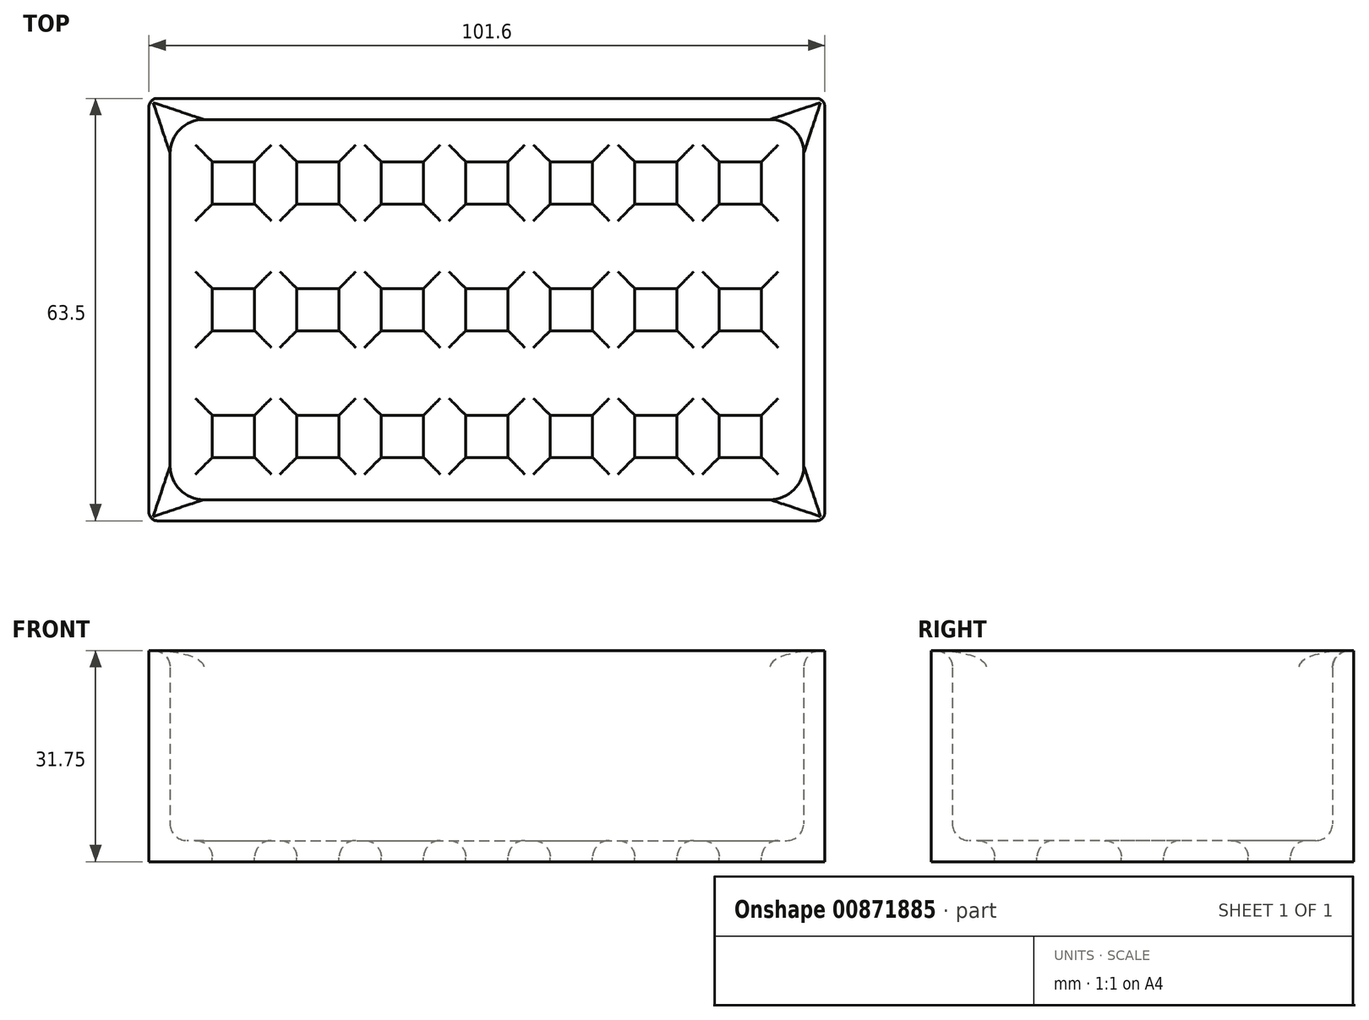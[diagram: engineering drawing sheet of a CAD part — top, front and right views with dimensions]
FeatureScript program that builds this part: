
annotation { "Feature Type Name" : "Feature", "Feature Type Description" : "" }
export const myFeature = defineFeature(function(context is Context, id is Id, definition is map)
    precondition{}
    {
        {
            var Q0;
            Q0=qCreatedBy(makeId("Top.planeOp"),FACE);
            var sketch = newSketch(context, id + "F0", { "sketchPlane" : qUnion([Q0])});
            skLineSegment(sketch, "E0.bottom", {"start": v(0, 0) * mm, "end": v(101.6, 0) * mm});
            skLineSegment(sketch, "E0.top", {"start": v(0, 63.5) * mm, "end": v(101.6, 63.5) * mm});
            skLineSegment(sketch, "E0.left", {"start": v(0, 0) * mm, "end": v(0, 63.5) * mm});
            skLineSegment(sketch, "E0.right", {"start": v(101.6, 0) * mm, "end": v(101.6, 63.5) * mm});
            skSolve(sketch);
        }
        {
            var Q0;
            Q0 = qSketchRegion(id + "F0", true);
            extrude(context, id + "F1", {"entities" : qUnion([Q0]), "depth" : 3.17 * mm, "offsetDistance" : 25.4 * mm});
        }
        {
            var Q0;
            Q0=makeQuery(id+"F1.opExtrude","CAP_FACE",FACE,{"disambiguationData":[OSD([sQuery(id+"F0.wireOp",EDGE,"E0.bottom"),sQuery(id+"F0.wireOp",EDGE,"E0.top"),sQuery(id+"F0.wireOp",EDGE,"E0.left"),sQuery(id+"F0.wireOp",EDGE,"E0.right")])],"isStart":false});
            var sketch = newSketch(context, id + "F2", { "sketchPlane" : qUnion([Q0])});
            skLineSegment(sketch, "E1.bottom", {"start": v(0, 63.5) * mm, "end": v(101.6, 63.5) * mm});
            skLineSegment(sketch, "E1.top", {"start": v(0, 0) * mm, "end": v(101.6, 0) * mm});
            skLineSegment(sketch, "E1.left", {"start": v(0, 63.5) * mm, "end": v(0, 0) * mm});
            skLineSegment(sketch, "E1.right", {"start": v(101.6, 63.5) * mm, "end": v(101.6, 0) * mm});
            skLineSegment(sketch, "E2.bottom", {"start": v(3.17, 60.33) * mm, "end": v(98.43, 60.33) * mm});
            skLineSegment(sketch, "E2.top", {"start": v(3.18, 3.18) * mm, "end": v(98.43, 3.18) * mm});
            skLineSegment(sketch, "E2.left", {"start": v(3.17, 60.33) * mm, "end": v(3.17, 3.17) * mm});
            skLineSegment(sketch, "E2.right", {"start": v(98.43, 60.33) * mm, "end": v(98.43, 3.18) * mm});
            skSolve(sketch);
        }
        {
            var Q0;
            Q0 = qSketchRegion(id + "F2", true);
            extrude(context, id + "F3", {"entities" : qUnion([Q0]), "operationType" : NewBodyOperationType.ADD, "depth" : 28.57 * mm, "offsetDistance" : 25.4 * mm});
        }
        {
            var Q0;
            Q0=makeQuery(id+"F3.opExtrude","CAP_EDGE",EDGE,{"disambiguationData":[OSD([sQuery(id+"F2.wireOp",EDGE,"E2.left")])],"isStart":false});
            var Q1;
            Q1=makeQuery(id+"F3.opExtrude","CAP_EDGE",EDGE,{"disambiguationData":[OSD([sQuery(id+"F2.wireOp",EDGE,"E2.bottom")])],"isStart":false});
            var Q2;
            Q2=makeQuery(id+"F3.opExtrude","CAP_EDGE",EDGE,{"disambiguationData":[OSD([sQuery(id+"F2.wireOp",EDGE,"E2.right")])],"isStart":false});
            var Q3;
            Q3=makeQuery(id+"F3.opExtrude","CAP_EDGE",EDGE,{"disambiguationData":[OSD([sQuery(id+"F2.wireOp",EDGE,"E2.top")])],"isStart":false});
            fillet(context, id + "F4", {"entities" : qUnion([Q0, Q1, Q2, Q3]), "radius" : 2.54 * mm, "tangentPropagation" : true, "allowEdgeOverflow" : false});
        }
        {
            var Q0;
            Q0=makeQuery(id+"F1.opExtrude","CAP_FACE",FACE,{"disambiguationData":[OSD([sQuery(id+"F0.wireOp",EDGE,"E0.bottom"),sQuery(id+"F0.wireOp",EDGE,"E0.top"),sQuery(id+"F0.wireOp",EDGE,"E0.left"),sQuery(id+"F0.wireOp",EDGE,"E0.right")])],"isStart":false});
            var sketch = newSketch(context, id + "F5", { "sketchPlane" : qUnion([Q0])});
            skLineSegment(sketch, "E3.bottom", {"start": v(9.53, 53.97) * mm, "end": v(15.88, 53.97) * mm});
            skLineSegment(sketch, "E3.top", {"start": v(9.53, 47.62) * mm, "end": v(15.88, 47.62) * mm});
            skLineSegment(sketch, "E3.left", {"start": v(9.53, 53.97) * mm, "end": v(9.53, 47.62) * mm});
            skLineSegment(sketch, "E3.right", {"start": v(15.88, 53.97) * mm, "end": v(15.88, 47.62) * mm});
            skLineSegment(sketch, "E4.1.0.0", {"start": v(28.58, 53.97) * mm, "end": v(28.58, 47.62) * mm});
            skLineSegment(sketch, "E4.1.0.1", {"start": v(22.23, 53.97) * mm, "end": v(28.57, 53.97) * mm});
            skLineSegment(sketch, "E4.1.0.2", {"start": v(22.23, 53.97) * mm, "end": v(22.23, 47.62) * mm});
            skLineSegment(sketch, "E4.1.0.3", {"start": v(22.23, 47.62) * mm, "end": v(28.57, 47.62) * mm});
            skLineSegment(sketch, "E4.2.0.0", {"start": v(41.28, 53.97) * mm, "end": v(41.28, 47.62) * mm});
            skLineSegment(sketch, "E4.2.0.1", {"start": v(34.92, 53.97) * mm, "end": v(41.27, 53.97) * mm});
            skLineSegment(sketch, "E4.2.0.2", {"start": v(34.92, 53.97) * mm, "end": v(34.92, 47.62) * mm});
            skLineSegment(sketch, "E4.2.0.3", {"start": v(34.92, 47.62) * mm, "end": v(41.27, 47.62) * mm});
            skLineSegment(sketch, "E4.3.0.0", {"start": v(53.97, 53.97) * mm, "end": v(53.97, 47.62) * mm});
            skLineSegment(sketch, "E4.3.0.1", {"start": v(47.62, 53.97) * mm, "end": v(53.97, 53.97) * mm});
            skLineSegment(sketch, "E4.3.0.2", {"start": v(47.62, 53.97) * mm, "end": v(47.62, 47.62) * mm});
            skLineSegment(sketch, "E4.3.0.3", {"start": v(47.62, 47.62) * mm, "end": v(53.97, 47.62) * mm});
            skLineSegment(sketch, "E4.4.0.0", {"start": v(66.67, 53.97) * mm, "end": v(66.67, 47.62) * mm});
            skLineSegment(sketch, "E4.4.0.1", {"start": v(60.32, 53.97) * mm, "end": v(66.67, 53.97) * mm});
            skLineSegment(sketch, "E4.4.0.2", {"start": v(60.32, 53.97) * mm, "end": v(60.32, 47.62) * mm});
            skLineSegment(sketch, "E4.4.0.3", {"start": v(60.32, 47.62) * mm, "end": v(66.67, 47.62) * mm});
            skLineSegment(sketch, "E4.5.0.0", {"start": v(79.38, 53.97) * mm, "end": v(79.38, 47.62) * mm});
            skLineSegment(sketch, "E4.5.0.1", {"start": v(73.03, 53.97) * mm, "end": v(79.38, 53.97) * mm});
            skLineSegment(sketch, "E4.5.0.2", {"start": v(73.03, 53.97) * mm, "end": v(73.03, 47.62) * mm});
            skLineSegment(sketch, "E4.5.0.3", {"start": v(73.03, 47.62) * mm, "end": v(79.38, 47.62) * mm});
            skLineSegment(sketch, "E4.6.0.0", {"start": v(92.07, 53.97) * mm, "end": v(92.07, 47.62) * mm});
            skLineSegment(sketch, "E4.6.0.1", {"start": v(85.72, 53.97) * mm, "end": v(92.07, 53.97) * mm});
            skLineSegment(sketch, "E4.6.0.2", {"start": v(85.72, 53.97) * mm, "end": v(85.72, 47.62) * mm});
            skLineSegment(sketch, "E4.6.0.3", {"start": v(85.72, 47.62) * mm, "end": v(92.07, 47.62) * mm});
            skLineSegment(sketch, "E4.direction1", {"start": v(15.88, 47.62) * mm, "end": v(28.58, 47.62) * mm, "construction": true});
            skLineSegment(sketch, "E5.1.0.0", {"start": v(28.58, 34.92) * mm, "end": v(28.58, 28.57) * mm});
            skLineSegment(sketch, "E5.1.0.1", {"start": v(15.88, 34.92) * mm, "end": v(15.88, 28.57) * mm});
            skLineSegment(sketch, "E5.1.0.2", {"start": v(73.02, 28.57) * mm, "end": v(79.38, 28.57) * mm});
            skLineSegment(sketch, "E5.1.0.3", {"start": v(47.62, 28.57) * mm, "end": v(53.97, 28.57) * mm});
            skLineSegment(sketch, "E5.1.0.4", {"start": v(73.03, 34.92) * mm, "end": v(79.38, 34.92) * mm});
            skLineSegment(sketch, "E5.1.0.5", {"start": v(66.67, 34.92) * mm, "end": v(66.67, 28.57) * mm});
            skLineSegment(sketch, "E5.1.0.6", {"start": v(9.53, 34.92) * mm, "end": v(9.53, 28.57) * mm});
            skLineSegment(sketch, "E5.1.0.7", {"start": v(47.62, 34.92) * mm, "end": v(53.97, 34.92) * mm});
            skLineSegment(sketch, "E5.1.0.8", {"start": v(9.52, 28.57) * mm, "end": v(15.88, 28.57) * mm});
            skLineSegment(sketch, "E5.1.0.9", {"start": v(53.97, 34.92) * mm, "end": v(53.97, 28.57) * mm});
            skLineSegment(sketch, "E5.1.0.10", {"start": v(34.92, 34.92) * mm, "end": v(34.92, 28.57) * mm});
            skLineSegment(sketch, "E5.1.0.11", {"start": v(60.32, 34.92) * mm, "end": v(60.32, 28.57) * mm});
            skLineSegment(sketch, "E5.1.0.12", {"start": v(60.32, 28.57) * mm, "end": v(66.67, 28.57) * mm});
            skLineSegment(sketch, "E5.1.0.13", {"start": v(85.72, 28.57) * mm, "end": v(92.07, 28.57) * mm});
            skLineSegment(sketch, "E5.1.0.14", {"start": v(41.28, 34.92) * mm, "end": v(41.28, 28.57) * mm});
            skLineSegment(sketch, "E5.1.0.15", {"start": v(15.88, 28.57) * mm, "end": v(28.58, 28.57) * mm, "construction": true});
            skLineSegment(sketch, "E5.1.0.16", {"start": v(34.92, 28.57) * mm, "end": v(41.28, 28.57) * mm});
            skLineSegment(sketch, "E5.1.0.17", {"start": v(34.92, 34.92) * mm, "end": v(41.28, 34.92) * mm});
            skLineSegment(sketch, "E5.1.0.18", {"start": v(9.53, 34.92) * mm, "end": v(15.88, 34.92) * mm});
            skLineSegment(sketch, "E5.1.0.19", {"start": v(85.72, 34.92) * mm, "end": v(92.07, 34.92) * mm});
            skLineSegment(sketch, "E5.1.0.20", {"start": v(60.33, 34.92) * mm, "end": v(66.67, 34.92) * mm});
            skLineSegment(sketch, "E5.1.0.21", {"start": v(73.03, 34.92) * mm, "end": v(73.03, 28.57) * mm});
            skLineSegment(sketch, "E5.1.0.22", {"start": v(85.72, 34.92) * mm, "end": v(85.72, 28.57) * mm});
            skLineSegment(sketch, "E5.1.0.23", {"start": v(22.23, 34.92) * mm, "end": v(28.58, 34.92) * mm});
            skLineSegment(sketch, "E5.1.0.24", {"start": v(79.38, 34.92) * mm, "end": v(79.38, 28.57) * mm});
            skLineSegment(sketch, "E5.1.0.25", {"start": v(22.23, 34.92) * mm, "end": v(22.23, 28.57) * mm});
            skLineSegment(sketch, "E5.1.0.26", {"start": v(92.07, 34.92) * mm, "end": v(92.07, 28.57) * mm});
            skLineSegment(sketch, "E5.1.0.27", {"start": v(47.62, 34.92) * mm, "end": v(47.62, 28.57) * mm});
            skLineSegment(sketch, "E5.1.0.28", {"start": v(22.22, 28.57) * mm, "end": v(28.58, 28.57) * mm});
            skLineSegment(sketch, "E5.2.0.0", {"start": v(28.58, 15.87) * mm, "end": v(28.58, 9.52) * mm});
            skLineSegment(sketch, "E5.2.0.1", {"start": v(15.88, 15.87) * mm, "end": v(15.88, 9.52) * mm});
            skLineSegment(sketch, "E5.2.0.2", {"start": v(73.02, 9.52) * mm, "end": v(79.38, 9.52) * mm});
            skLineSegment(sketch, "E5.2.0.3", {"start": v(47.62, 9.52) * mm, "end": v(53.97, 9.52) * mm});
            skLineSegment(sketch, "E5.2.0.4", {"start": v(73.03, 15.87) * mm, "end": v(79.38, 15.87) * mm});
            skLineSegment(sketch, "E5.2.0.5", {"start": v(66.67, 15.87) * mm, "end": v(66.67, 9.52) * mm});
            skLineSegment(sketch, "E5.2.0.6", {"start": v(9.53, 15.87) * mm, "end": v(9.53, 9.52) * mm});
            skLineSegment(sketch, "E5.2.0.7", {"start": v(47.62, 15.87) * mm, "end": v(53.97, 15.87) * mm});
            skLineSegment(sketch, "E5.2.0.8", {"start": v(9.53, 9.52) * mm, "end": v(15.88, 9.52) * mm});
            skLineSegment(sketch, "E5.2.0.9", {"start": v(53.97, 15.87) * mm, "end": v(53.97, 9.52) * mm});
            skLineSegment(sketch, "E5.2.0.10", {"start": v(34.92, 15.87) * mm, "end": v(34.92, 9.52) * mm});
            skLineSegment(sketch, "E5.2.0.11", {"start": v(60.32, 15.87) * mm, "end": v(60.32, 9.52) * mm});
            skLineSegment(sketch, "E5.2.0.12", {"start": v(60.32, 9.52) * mm, "end": v(66.67, 9.52) * mm});
            skLineSegment(sketch, "E5.2.0.13", {"start": v(85.72, 9.52) * mm, "end": v(92.07, 9.52) * mm});
            skLineSegment(sketch, "E5.2.0.14", {"start": v(41.28, 15.87) * mm, "end": v(41.28, 9.52) * mm});
            skLineSegment(sketch, "E5.2.0.15", {"start": v(15.88, 9.52) * mm, "end": v(28.58, 9.52) * mm, "construction": true});
            skLineSegment(sketch, "E5.2.0.16", {"start": v(34.92, 9.52) * mm, "end": v(41.28, 9.52) * mm});
            skLineSegment(sketch, "E5.2.0.17", {"start": v(34.92, 15.87) * mm, "end": v(41.28, 15.87) * mm});
            skLineSegment(sketch, "E5.2.0.18", {"start": v(9.53, 15.87) * mm, "end": v(15.88, 15.87) * mm});
            skLineSegment(sketch, "E5.2.0.19", {"start": v(85.72, 15.87) * mm, "end": v(92.07, 15.87) * mm});
            skLineSegment(sketch, "E5.2.0.20", {"start": v(60.33, 15.87) * mm, "end": v(66.67, 15.87) * mm});
            skLineSegment(sketch, "E5.2.0.21", {"start": v(73.03, 15.87) * mm, "end": v(73.03, 9.52) * mm});
            skLineSegment(sketch, "E5.2.0.22", {"start": v(85.72, 15.87) * mm, "end": v(85.72, 9.52) * mm});
            skLineSegment(sketch, "E5.2.0.23", {"start": v(22.23, 15.87) * mm, "end": v(28.58, 15.87) * mm});
            skLineSegment(sketch, "E5.2.0.24", {"start": v(79.38, 15.87) * mm, "end": v(79.38, 9.52) * mm});
            skLineSegment(sketch, "E5.2.0.25", {"start": v(22.23, 15.87) * mm, "end": v(22.23, 9.52) * mm});
            skLineSegment(sketch, "E5.2.0.26", {"start": v(92.07, 15.87) * mm, "end": v(92.07, 9.52) * mm});
            skLineSegment(sketch, "E5.2.0.27", {"start": v(47.62, 15.87) * mm, "end": v(47.62, 9.52) * mm});
            skLineSegment(sketch, "E5.2.0.28", {"start": v(22.22, 9.52) * mm, "end": v(28.58, 9.52) * mm});
            skLineSegment(sketch, "E5.direction1", {"start": v(9.53, 47.62) * mm, "end": v(9.53, 28.57) * mm, "construction": true});
            skSolve(sketch);
        }
        {
            var Q0;
            Q0 = qSketchRegion(id + "F5", true);
            extrude(context, id + "F6", {"entities" : qUnion([Q0]), "operationType" : NewBodyOperationType.REMOVE, "endBound" : BoundingType.THROUGH_ALL, "oppositeDirection" : true, "depth" : 25.4 * mm, "offsetDistance" : 25.4 * mm});
        }
        {
            var Q0;
            Q0=makeQuery(id+"F6.boolean.opBoolean","COPY",EDGE,{"derivedFrom":makeQuery(id+"F6.opExtrude","CAP_EDGE",EDGE,{"disambiguationData":[OSD([sQuery(id+"F5.wireOp",EDGE,"E3.top")])],"isStart":true})});
            var Q1;
            Q1=makeQuery(id+"F6.boolean.opBoolean","COPY",EDGE,{"derivedFrom":makeQuery(id+"F6.opExtrude","CAP_EDGE",EDGE,{"disambiguationData":[OSD([sQuery(id+"F5.wireOp",EDGE,"E3.left")])],"isStart":true})});
            var Q2;
            Q2=makeQuery(id+"F6.boolean.opBoolean","COPY",EDGE,{"derivedFrom":makeQuery(id+"F6.opExtrude","CAP_EDGE",EDGE,{"disambiguationData":[OSD([sQuery(id+"F5.wireOp",EDGE,"E3.bottom")])],"isStart":true})});
            var Q3;
            Q3=makeQuery(id+"F6.boolean.opBoolean","COPY",EDGE,{"derivedFrom":makeQuery(id+"F6.opExtrude","CAP_EDGE",EDGE,{"disambiguationData":[OSD([sQuery(id+"F5.wireOp",EDGE,"E3.right")])],"isStart":true})});
            var Q4;
            Q4=makeQuery(id+"F6.boolean.opBoolean","COPY",EDGE,{"derivedFrom":makeQuery(id+"F6.opExtrude","CAP_EDGE",EDGE,{"disambiguationData":[OSD([sQuery(id+"F5.wireOp",EDGE,"E4.1.0.2")])],"isStart":true})});
            var Q5;
            Q5=makeQuery(id+"F6.boolean.opBoolean","COPY",EDGE,{"derivedFrom":makeQuery(id+"F6.opExtrude","CAP_EDGE",EDGE,{"disambiguationData":[OSD([sQuery(id+"F5.wireOp",EDGE,"E4.1.0.1")])],"isStart":true})});
            var Q6;
            Q6=makeQuery(id+"F6.boolean.opBoolean","COPY",EDGE,{"derivedFrom":makeQuery(id+"F6.opExtrude","CAP_EDGE",EDGE,{"disambiguationData":[OSD([sQuery(id+"F5.wireOp",EDGE,"E4.1.0.0")])],"isStart":true})});
            var Q7;
            Q7=makeQuery(id+"F1.opExtrude","CAP_FACE",FACE,{"disambiguationData":[OSD([sQuery(id+"F0.wireOp",EDGE,"E0.bottom"),sQuery(id+"F0.wireOp",EDGE,"E0.top"),sQuery(id+"F0.wireOp",EDGE,"E0.left"),sQuery(id+"F0.wireOp",EDGE,"E0.right")])],"isStart":false});
            var Q8;
            Q8=makeQuery(id+"F6.boolean.opBoolean","COPY",EDGE,{"derivedFrom":makeQuery(id+"F6.opExtrude","CAP_EDGE",EDGE,{"disambiguationData":[OSD([sQuery(id+"F5.wireOp",EDGE,"E4.1.0.3")])],"isStart":true})});
            fillet(context, id + "F7", {"entities" : qUnion([Q0, Q1, Q2, Q3, Q4, Q5, Q6, Q7, Q8]), "radius" : 2.54 * mm, "tangentPropagation" : true, "allowEdgeOverflow" : false});
        }
        {
            var Q0;
            Q0=makeQuery(id+"F3.opExtrude","SWEPT_EDGE",EDGE,{"disambiguationData":[OSD([sQuery(id+"F2.wireOp",EDGE,"E2.bottom"),sQuery(id+"F2.wireOp",EDGE,"E2.left")])]});
            var Q1;
            Q1=makeQuery(id+"F3.opExtrude","SWEPT_EDGE",EDGE,{"disambiguationData":[OSD([sQuery(id+"F2.wireOp",EDGE,"E2.bottom"),sQuery(id+"F2.wireOp",EDGE,"E2.right")])]});
            var Q2;
            Q2=makeQuery(id+"F3.opExtrude","SWEPT_EDGE",EDGE,{"disambiguationData":[OSD([sQuery(id+"F2.wireOp",EDGE,"E2.top"),sQuery(id+"F2.wireOp",EDGE,"E2.right")])]});
            var Q3;
            Q3=makeQuery(id+"F3.opExtrude","SWEPT_EDGE",EDGE,{"disambiguationData":[OSD([sQuery(id+"F2.wireOp",EDGE,"E2.top"),sQuery(id+"F2.wireOp",EDGE,"E2.left")])]});
            fillet(context, id + "F8", {"entities" : qUnion([Q0, Q1, Q2, Q3]), "radius" : 5.08 * mm, "tangentPropagation" : true, "allowEdgeOverflow" : false});
        }
        {
            var Q0;
            Q0=makeQuery(id+"F3.boolean.opBoolean","MERGE",EDGE,{"derivedFrom":[makeQuery(id+"F1.opExtrude","SWEPT_EDGE",EDGE,{"disambiguationData":[OSD([sQuery(id+"F0.wireOp",EDGE,"E0.top"),sQuery(id+"F0.wireOp",EDGE,"E0.left")])]}),makeQuery(id+"F3.opExtrude","SWEPT_EDGE",EDGE,{"disambiguationData":[OSD([sQuery(id+"F2.wireOp",EDGE,"E1.bottom"),sQuery(id+"F2.wireOp",EDGE,"E1.left")])]})]});
            var Q1;
            Q1=makeQuery(id+"F3.boolean.opBoolean","MERGE",EDGE,{"derivedFrom":[makeQuery(id+"F1.opExtrude","SWEPT_EDGE",EDGE,{"disambiguationData":[OSD([sQuery(id+"F0.wireOp",EDGE,"E0.bottom"),sQuery(id+"F0.wireOp",EDGE,"E0.left")])]}),makeQuery(id+"F3.opExtrude","SWEPT_EDGE",EDGE,{"disambiguationData":[OSD([sQuery(id+"F2.wireOp",EDGE,"E1.top"),sQuery(id+"F2.wireOp",EDGE,"E1.left")])]})]});
            var Q2;
            Q2=makeQuery(id+"F3.boolean.opBoolean","MERGE",EDGE,{"derivedFrom":[makeQuery(id+"F1.opExtrude","SWEPT_EDGE",EDGE,{"disambiguationData":[OSD([sQuery(id+"F0.wireOp",EDGE,"E0.bottom"),sQuery(id+"F0.wireOp",EDGE,"E0.right")])]}),makeQuery(id+"F3.opExtrude","SWEPT_EDGE",EDGE,{"disambiguationData":[OSD([sQuery(id+"F2.wireOp",EDGE,"E1.top"),sQuery(id+"F2.wireOp",EDGE,"E1.right")])]})]});
            var Q3;
            Q3=makeQuery(id+"F3.boolean.opBoolean","MERGE",EDGE,{"derivedFrom":[makeQuery(id+"F1.opExtrude","SWEPT_EDGE",EDGE,{"disambiguationData":[OSD([sQuery(id+"F0.wireOp",EDGE,"E0.top"),sQuery(id+"F0.wireOp",EDGE,"E0.right")])]}),makeQuery(id+"F3.opExtrude","SWEPT_EDGE",EDGE,{"disambiguationData":[OSD([sQuery(id+"F2.wireOp",EDGE,"E1.bottom"),sQuery(id+"F2.wireOp",EDGE,"E1.right")])]})]});
            fillet(context, id + "F9", {"entities" : qUnion([Q0, Q1, Q2, Q3]), "radius" : 1.27 * mm, "tangentPropagation" : true, "allowEdgeOverflow" : false});
        }
    });
